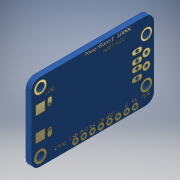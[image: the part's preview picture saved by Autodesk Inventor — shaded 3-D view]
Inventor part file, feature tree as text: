
AUTODESK INVENTOR PART (.ipt)
format: ipt  version: 2018 (Build 220112000, 112)  size: 2,540,544 bytes
history: native  units: mm
features: other x7, extrude x3, hole x3, sketch x2, projected_geometry x1
ambient origin geometry x8: Origin, YZ Plane, XZ Plane, XY Plane, X Axis, Y Axis, Z Axis, Center Point
bodies: Body1 (feature_tree), Body2 (feature_tree), Body3 (feature_tree)
feature tree (16):
  other  "PCB"
  other  "PlanoCurre"
  other  "FOTO_PLANO"
  sketch  "BocetoPCB"  dims[d129=2.4mm d130=6.0mm d131=4.0mm d132=2.0mm d133=90.0deg d134=8.0mm d135=20.594885mm d138=0.02mm d139=0.0mm d144=1.0mm d145=6.0mm d146=4.0mm d147=2.0mm d148=90.0deg d149=8.0mm d150=20.594885mm d151=1.0mm d152=6.0mm d153=4.0mm d154=2.0mm d155=90.0deg d156=8.0mm d157=20.594885mm d325=0.03mm d326=0.0mm]
  extrude  "board"  Depth=0.02mm TaperAngle=0.0deg
  hole  "Agujeros"  [1 undecoded]
  sketch  "Boceto4"  dims[d127=1.588mm d128=0.0mm]
  extrude  "Extrusión3"  [1 undecoded]
  hole  "Agujero4"  [1 undecoded]
  hole  "Agujero5"  [1 undecoded]
  extrude  "Extrusión6"  [1 undecoded]
  other  "PADS"
  projected_geometry  "Contorno proyectado1"
  other  "textos"
  other  "comps"
  other  "letras"
note: 5 required parameter values undecoded (feature->parameter linkage not recoverable at this tier; creation-order binding heuristic only, values carry confidence <= 0.55)
